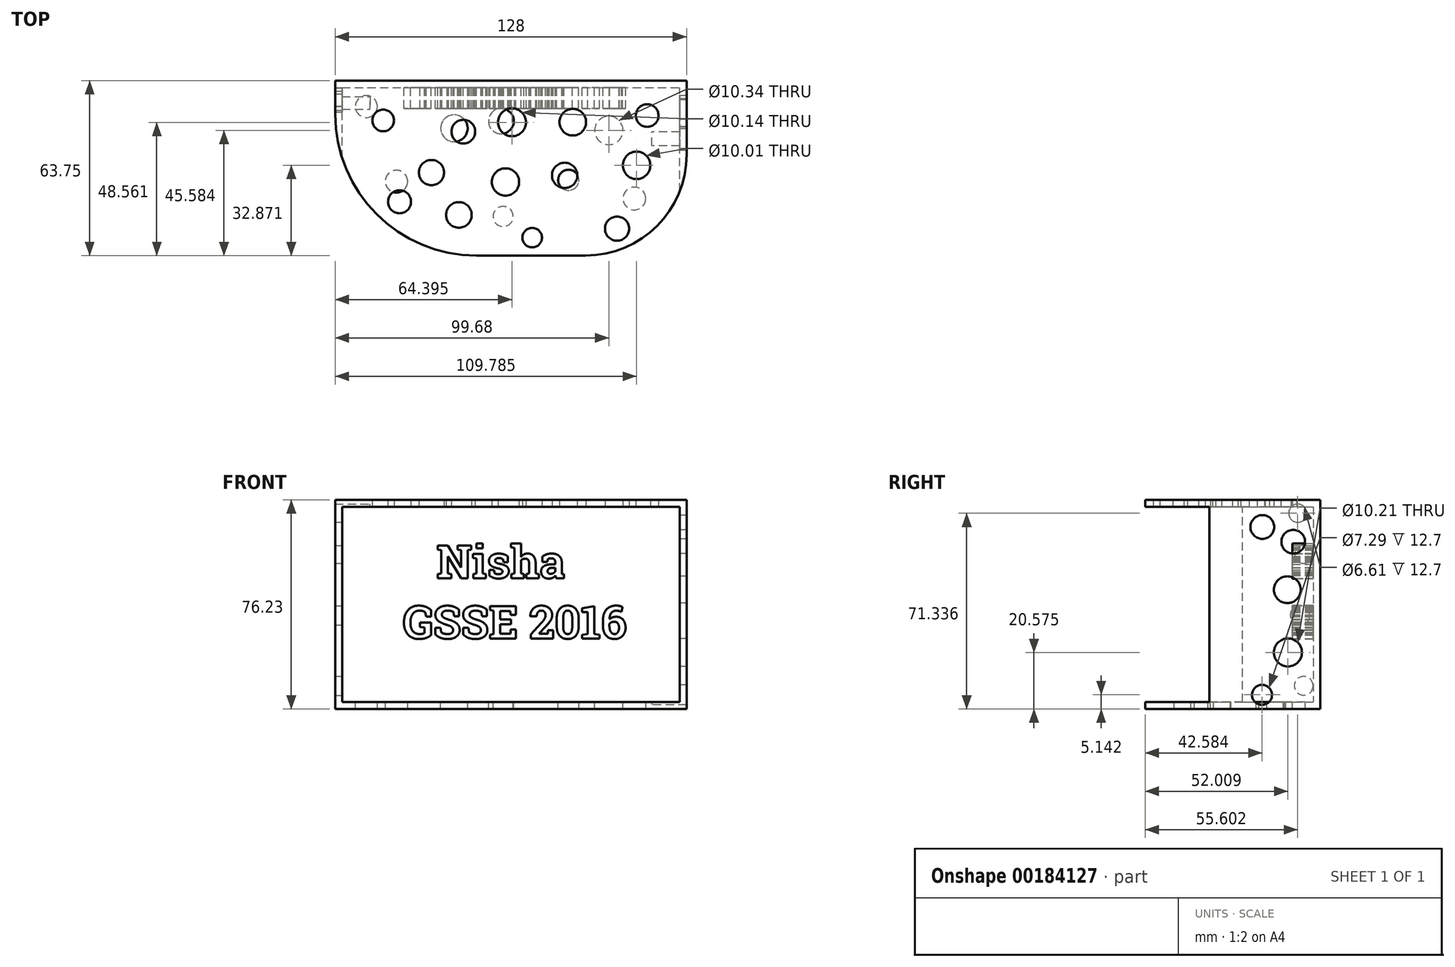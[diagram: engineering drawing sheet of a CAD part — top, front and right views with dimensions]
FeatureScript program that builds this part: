
annotation { "Feature Type Name" : "Feature", "Feature Type Description" : "" }
export const myFeature = defineFeature(function(context is Context, id is Id, definition is map)
    precondition{}
    {
        {
            var Q0;
            Q0=qCreatedBy(makeId("Front.planeOp"),FACE);
            var sketch = newSketch(context, id + "F0", { "sketchPlane" : qUnion([Q0])});
            skLineSegment(sketch, "E0.bottom", {"start": v(-63.4, 36.51) * mm, "end": v(64.6, 36.51) * mm});
            skLineSegment(sketch, "E0.top", {"start": v(-63.4, -39.72) * mm, "end": v(64.6, -39.72) * mm});
            skLineSegment(sketch, "E0.left", {"start": v(-63.4, 36.51) * mm, "end": v(-63.4, -39.72) * mm});
            skLineSegment(sketch, "E0.right", {"start": v(64.6, 36.51) * mm, "end": v(64.6, -39.72) * mm});
            skSolve(sketch);
        }
        {
            var Q0;
            Q0=makeQuery(id+"F0.imprint","IMPRINT",FACE,{"disambiguationData":[TD([[makeQuery(id+"F0.imprint","IMPRINT",EDGE,{"derivedFrom":sQuery(id+"F0.wireOp",EDGE,"E0.bottom")}),-1.0]])]});
            extrude(context, id + "F1", {"entities" : qUnion([Q0]), "depth" : 63.75 * mm});
        }
        {
            var Q0;
            Q0=makeQuery(id+"F1.opExtrude","CAP_FACE",FACE,{"disambiguationData":[OSD([sQuery(id+"F0.wireOp",EDGE,"E0.bottom"),sQuery(id+"F0.wireOp",EDGE,"E0.top"),sQuery(id+"F0.wireOp",EDGE,"E0.left"),sQuery(id+"F0.wireOp",EDGE,"E0.right")])],"isStart":false});
            var Q1;
            Q1=makeQuery(id+"F1.opExtrude","SWEPT_BODY",BODY,{"disambiguationData":[OSD([sQuery(id+"F0.wireOp",EDGE,"E0.bottom"),sQuery(id+"F0.wireOp",EDGE,"E0.top"),sQuery(id+"F0.wireOp",EDGE,"E0.left"),sQuery(id+"F0.wireOp",EDGE,"E0.right")])]});
            shell(context, id + "F2", {"entities" : qUnion([Q0]), "parts" : qUnion([Q1]), "thickness" : 2.54 * mm});
        }
        {
            var Q0;
            Q0=makeQuery(id+"F1.opExtrude","CAP_EDGE",EDGE,{"disambiguationData":[OSD([sQuery(id+"F0.wireOp",EDGE,"E0.left")])],"isStart":false});
            fillet(context, id + "F3", {"entities" : qUnion([Q0]), "radius" : 51.5 * mm, "tangentPropagation" : true, "allowEdgeOverflow" : false});
        }
        {
            var Q0;
            Q0=makeQuery(id+"F1.opExtrude","CAP_EDGE",EDGE,{"disambiguationData":[OSD([sQuery(id+"F0.wireOp",EDGE,"E0.right")])],"isStart":false});
            fillet(context, id + "F4", {"entities" : qUnion([Q0]), "radius" : 36.8 * mm, "tangentPropagation" : true, "allowEdgeOverflow" : false});
        }
        {
            var Q0;
            Q0=makeQuery(id+"F1.opExtrude","SWEPT_FACE",FACE,{"disambiguationData":[OSD([sQuery(id+"F0.wireOp",EDGE,"E0.top")])]});
            var sketch = newSketch(context, id + "F5", { "sketchPlane" : qUnion([Q0])});
            skCircle(sketch, "E1", {"center": v(-41.08, 36.73) * mm, "radius": 4.07 * mm});
            skCircle(sketch, "E2", {"center": v(21.58, 36.23) * mm, "radius": 3.76 * mm});
            skCircle(sketch, "E3", {"center": v(-20.07, 17.37) * mm, "radius": 4.9 * mm});
            skCircle(sketch, "E4", {"center": v(36.27, 18.17) * mm, "radius": 5.17 * mm});
            skCircle(sketch, "E5", {"center": v(-2.22, 49.52) * mm, "radius": 3.66 * mm});
            skCircle(sketch, "E6", {"center": v(-52.05, 9.45) * mm, "radius": 4 * mm});
            skCircle(sketch, "E7", {"center": v(45.57, 42.96) * mm, "radius": 4.14 * mm});
            skCircle(sketch, "E8", {"center": v(-2.96, 14.78) * mm, "radius": 4.61 * mm});
            skSolve(sketch);
        }
        {
            var Q0;
            Q0 = qSketchRegion(id + "F5", true);
            extrude(context, id + "F6", {"entities" : qUnion([Q0]), "operationType" : NewBodyOperationType.REMOVE, "endBound" : BoundingType.SYMMETRIC, "depth" : 25.4 * mm});
        }
        {
            var Q0;
            Q0=makeQuery(id+"F1.opExtrude","SWEPT_FACE",FACE,{"disambiguationData":[OSD([sQuery(id+"F0.wireOp",EDGE,"E0.right")])]});
            var sketch = newSketch(context, id + "F7", { "sketchPlane" : qUnion([Q0])});
            skCircle(sketch, "E9", {"center": v(-21.17, -34.58) * mm, "radius": 3.64 * mm});
            skCircle(sketch, "E10", {"center": v(-21.05, 26.6) * mm, "radius": 4.33 * mm});
            skCircle(sketch, "E11", {"center": v(-11.93, 3.72) * mm, "radius": 4.88 * mm});
            skCircle(sketch, "E12", {"center": v(-11.74, -19.15) * mm, "radius": 5.1 * mm});
            skCircle(sketch, "E13", {"center": v(-9.8, 21.2) * mm, "radius": 4.31 * mm});
            skSolve(sketch);
        }
        {
            var Q0;
            Q0 = qSketchRegion(id + "F7", true);
            extrude(context, id + "F8", {"entities" : qUnion([Q0]), "operationType" : NewBodyOperationType.REMOVE, "endBound" : BoundingType.SYMMETRIC, "depth" : 25.4 * mm});
        }
        {
            var Q0;
            Q0=makeQuery(id+"F1.opExtrude","SWEPT_FACE",FACE,{"disambiguationData":[OSD([sQuery(id+"F0.wireOp",EDGE,"E0.bottom")])]});
            var sketch = newSketch(context, id + "F9", { "sketchPlane" : qUnion([Q0])});
            skCircle(sketch, "E14", {"center": v(39.25, -53.95) * mm, "radius": 4.4 * mm});
            skCircle(sketch, "E15", {"center": v(20.17, -34.53) * mm, "radius": 4.62 * mm});
            skCircle(sketch, "E16", {"center": v(46.38, -30.88) * mm, "radius": 5 * mm});
            skCircle(sketch, "E17", {"center": v(23.14, -15.14) * mm, "radius": 4.85 * mm});
            skCircle(sketch, "E18", {"center": v(50.22, -12.73) * mm, "radius": 4.13 * mm});
            skCircle(sketch, "E19", {"center": v(-18.36, -48.95) * mm, "radius": 4.67 * mm});
            skCircle(sketch, "E20", {"center": v(-16.73, -18.6) * mm, "radius": 4.32 * mm});
            skCircle(sketch, "E21", {"center": v(8.35, -57.21) * mm, "radius": 3.56 * mm});
            skCircle(sketch, "E22", {"center": v(-45.93, -14.52) * mm, "radius": 3.95 * mm});
            skCircle(sketch, "E23", {"center": v(-39.97, -44.15) * mm, "radius": 4.2 * mm});
            skCircle(sketch, "E24", {"center": v(-28.34, -33.5) * mm, "radius": 4.6 * mm});
            skCircle(sketch, "E25", {"center": v(-1.37, -36.94) * mm, "radius": 4.97 * mm});
            skCircle(sketch, "E26", {"center": v(0.99, -15.19) * mm, "radius": 5.07 * mm});
            skSolve(sketch);
        }
        {
            var Q0;
            Q0 = qSketchRegion(id + "F9", true);
            extrude(context, id + "F10", {"entities" : qUnion([Q0]), "operationType" : NewBodyOperationType.REMOVE, "endBound" : BoundingType.SYMMETRIC, "depth" : 25.4 * mm});
        }
        {
            var Q0;
            Q0=makeQuery(id+"F1.opExtrude","SWEPT_FACE",FACE,{"disambiguationData":[OSD([sQuery(id+"F0.wireOp",EDGE,"E0.left")])]});
            var sketch = newSketch(context, id + "F11", { "sketchPlane" : qUnion([Q0])});
            skCircle(sketch, "E27", {"center": v(8.15, 31.62) * mm, "radius": 3.3 * mm});
            skCircle(sketch, "E28", {"center": v(5.99, 16.6) * mm, "radius": 3.29 * mm});
            skCircle(sketch, "E29", {"center": v(6, -31.28) * mm, "radius": 3.44 * mm});
            skCircle(sketch, "E30", {"center": v(7.32, -5.64) * mm, "radius": 3.54 * mm});
            skSolve(sketch);
        }
        {
            var Q0;
            Q0 = qSketchRegion(id + "F11", true);
            extrude(context, id + "F12", {"entities" : qUnion([Q0]), "operationType" : NewBodyOperationType.REMOVE, "endBound" : BoundingType.SYMMETRIC, "depth" : 25.4 * mm});
        }
        {
            var Q0;
            Q0=makeQuery(id+"F2.opShell","OFFSET_FACE",FACE,{"disambiguationData":[OSD([sQuery(id+"F0.wireOp",EDGE,"E0.bottom"),sQuery(id+"F0.wireOp",EDGE,"E0.top"),sQuery(id+"F0.wireOp",EDGE,"E0.left"),sQuery(id+"F0.wireOp",EDGE,"E0.right")])]});
            var sketch = newSketch(context, id + "F13", { "sketchPlane" : qUnion([Q0])});
            skText(sketch, "E31", { "text": "   Nisha\nGSSE 2016", "fontName": "RobotoSlab-Bold.ttf"});
            const initialGuessF13  = {"E31": [-0.03873, 0.00794, 1, 0, 0.01201]};
            skSetInitialGuess(sketch, initialGuessF13);
            skSolve(sketch);
        }
        {
            var Q0;
            Q0 = qSketchRegion(id + "F13", true);
            extrude(context, id + "F14", {"entities" : qUnion([Q0]), "operationType" : NewBodyOperationType.ADD, "depth" : 2.54 * mm});
        }
        {
            var Q0;
            Q0 = qSketchRegion(id + "F13", true);
            extrude(context, id + "F15", {"entities" : qUnion([Q0]), "operationType" : NewBodyOperationType.ADD, "depth" : 2.03 * mm});
        }
        {
            var Q0;
            Q0 = qSketchRegion(id + "F13", true);
            extrude(context, id + "F16", {"entities" : qUnion([Q0]), "operationType" : NewBodyOperationType.ADD, "depth" : 1.02 * mm});
        }
        {
            var Q0;
            Q0 = qSketchRegion(id + "F13", true);
            extrude(context, id + "F17", {"entities" : qUnion([Q0]), "operationType" : NewBodyOperationType.ADD, "depth" : 2.54 * mm});
        }
        {
            var Q0;
            Q0 = qSketchRegion(id + "F13", true);
            extrude(context, id + "F18", {"entities" : qUnion([Q0]), "operationType" : NewBodyOperationType.ADD, "depth" : 7.62 * mm});
        }
        {
            var Q0;
            Q0 = qSketchRegion(id + "F13", true);
            extrude(context, id + "F19", {"entities" : qUnion([Q0]), "operationType" : NewBodyOperationType.ADD, "depth" : 4.57 * mm});
        }
    });
